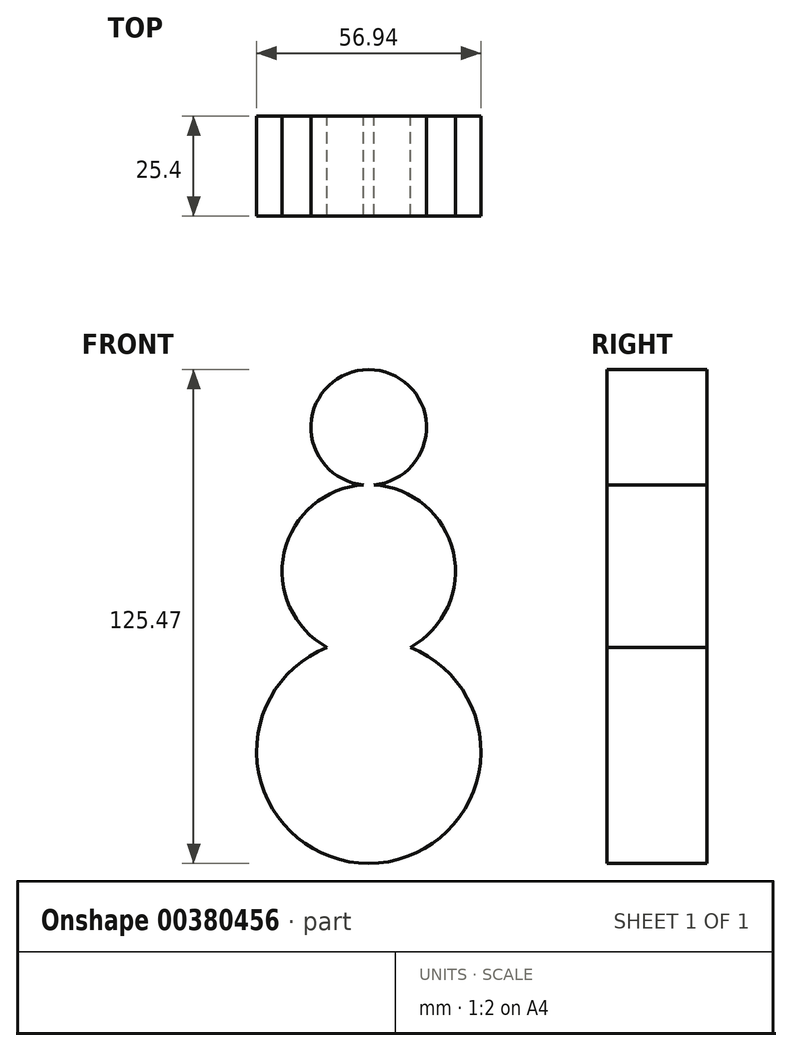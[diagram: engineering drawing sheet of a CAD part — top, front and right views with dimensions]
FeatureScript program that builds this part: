
annotation { "Feature Type Name" : "Feature", "Feature Type Description" : "" }
export const myFeature = defineFeature(function(context is Context, id is Id, definition is map)
    precondition{}
    {
        {
            var Q0;
            Q0=qCreatedBy(makeId("Front.planeOp"),FACE);
            var sketch = newSketch(context, id + "F0", { "sketchPlane" : qUnion([Q0])});
            skCircle(sketch, "E0", {"center": v(0, 0) * mm, "radius": 14.68 * mm});
            skCircle(sketch, "E1", {"center": v(0, -36.6) * mm, "radius": 22.02 * mm});
            skCircle(sketch, "E2", {"center": v(0, -82.32) * mm, "radius": 28.47 * mm});
            skSolve(sketch);
        }
        {
            var Q0;
            Q0 = qSketchRegion(id + "F0", true);
            extrude(context, id + "F1", {"entities" : qUnion([Q0]), "depth" : 25.4 * mm});
        }
    });
